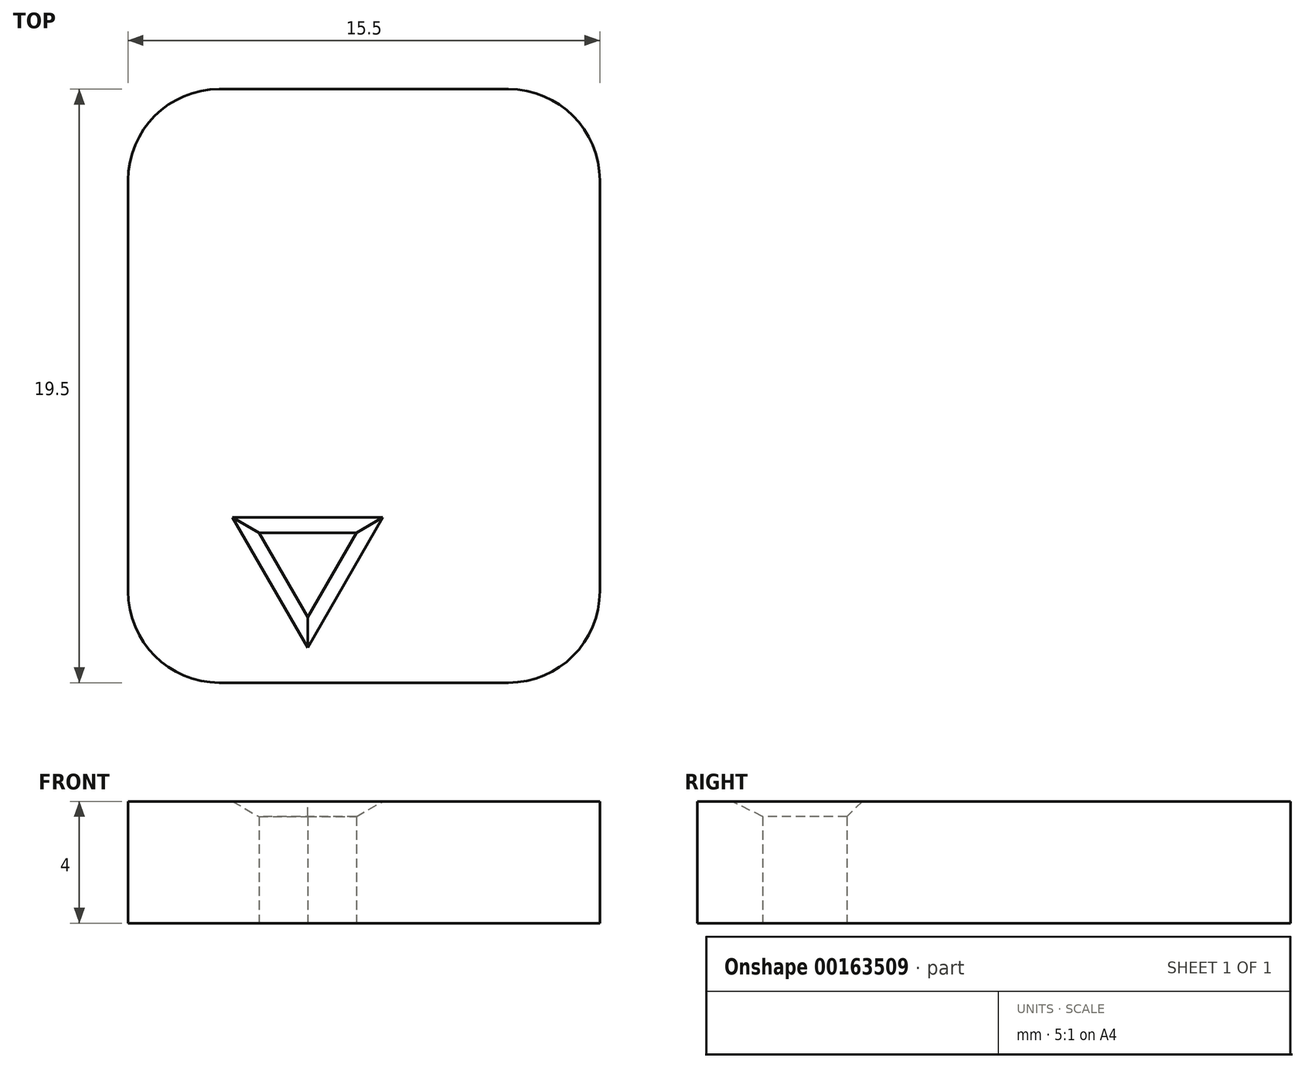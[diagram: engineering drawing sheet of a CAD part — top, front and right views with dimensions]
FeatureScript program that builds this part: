
annotation { "Feature Type Name" : "Feature", "Feature Type Description" : "" }
export const myFeature = defineFeature(function(context is Context, id is Id, definition is map)
    precondition{}
    {
        {
            var Q0;
            Q0=qCreatedBy(makeId("Top.planeOp"),FACE);
            var sketch = newSketch(context, id + "F0", { "sketchPlane" : qUnion([Q0])});
            skLineSegment(sketch, "E0.bottom", {"start": v(-15.5, 0) * mm, "end": v(0, 0) * mm});
            skLineSegment(sketch, "E0.top", {"start": v(-15.5, 19.5) * mm, "end": v(0, 19.5) * mm});
            skLineSegment(sketch, "E0.left", {"start": v(0, 0) * mm, "end": v(0, 19.5) * mm});
            skLineSegment(sketch, "E0.right", {"start": v(-15.5, 0) * mm, "end": v(-15.5, 19.5) * mm});
            skSolve(sketch);
        }
        {
            var Q0;
            Q0=qSketchRegion(id+"F0",true);
            extrude(context, id + "F1", {"entities" : qUnion([Q0]), "depth" : 4 * mm});
        }
        {
            var Q0;
            Q0=qCreatedBy(makeId("Top.planeOp"),FACE);
            var sketch = newSketch(context, id + "F2", { "sketchPlane" : qUnion([Q0])});
            skLineSegment(sketch, "E1.0", {"start": v(-15.5, 0) * mm, "end": v(-15.5, 19.5) * mm, "construction": true});
            skLineSegment(sketch, "E2", {"start": v(0, 4) * mm, "end": v(-15.5, 4) * mm, "construction": true});
            skLineSegment(sketch, "E3", {"start": v(-9.6, 0) * mm, "end": v(-9.6, 4) * mm, "construction": true});
            skCircle(sketch, "E4.cCircle", {"center": v(-9.6, 4) * mm, "radius": 1.85 * mm, "construction": true});
            skLineSegment(sketch, "E4.0", {"start": v(-9.6, 2.15) * mm, "end": v(-11.2, 4.93) * mm});
            skLineSegment(sketch, "E4.1", {"start": v(-11.2, 4.92) * mm, "end": v(-8, 4.92) * mm});
            skLineSegment(sketch, "E4.2", {"start": v(-8, 4.92) * mm, "end": v(-9.6, 2.15) * mm});
            skCircle(sketch, "E5", {"center": v(-9.6, 4) * mm, "radius": 1.5 * mm, "construction": true});
            skSolve(sketch);
        }
        {
            var Q0;
            Q0=qSketchRegion(id+"F2",true);
            extrude(context, id + "F3", {"entities" : qUnion([Q0]), "operationType" : NewBodyOperationType.REMOVE, "endBound" : BoundingType.THROUGH_ALL, "depth" : 25 * mm});
        }
        {
            var Q0;
            Q0=makeQuery(id+"F3.boolean.opBoolean","INTERSECT",EDGE,{"derivedFrom":[makeQuery(id+"F1.opExtrude","CAP_FACE",FACE,{"disambiguationData":[OSD([sQuery(id+"F0.wireOp",EDGE,"E0.bottom"),sQuery(id+"F0.wireOp",EDGE,"E0.top"),sQuery(id+"F0.wireOp",EDGE,"E0.left"),sQuery(id+"F0.wireOp",EDGE,"E0.right")])],"isStart":false}),makeQuery(id+"F3.opExtrude","SWEPT_FACE",FACE,{"disambiguationData":[OSD([sQuery(id+"F2.wireOp",EDGE,"E4.1")])]})]});
            var Q1;
            Q1=makeQuery(id+"F3.boolean.opBoolean","INTERSECT",EDGE,{"derivedFrom":[makeQuery(id+"F1.opExtrude","CAP_FACE",FACE,{"disambiguationData":[OSD([sQuery(id+"F0.wireOp",EDGE,"E0.bottom"),sQuery(id+"F0.wireOp",EDGE,"E0.top"),sQuery(id+"F0.wireOp",EDGE,"E0.left"),sQuery(id+"F0.wireOp",EDGE,"E0.right")])],"isStart":false}),makeQuery(id+"F3.opExtrude","SWEPT_FACE",FACE,{"disambiguationData":[OSD([sQuery(id+"F2.wireOp",EDGE,"E4.0")])]})]});
            var Q2;
            Q2=makeQuery(id+"F3.boolean.opBoolean","INTERSECT",EDGE,{"derivedFrom":[makeQuery(id+"F1.opExtrude","CAP_FACE",FACE,{"disambiguationData":[OSD([sQuery(id+"F0.wireOp",EDGE,"E0.bottom"),sQuery(id+"F0.wireOp",EDGE,"E0.top"),sQuery(id+"F0.wireOp",EDGE,"E0.left"),sQuery(id+"F0.wireOp",EDGE,"E0.right")])],"isStart":false}),makeQuery(id+"F3.opExtrude","SWEPT_FACE",FACE,{"disambiguationData":[OSD([sQuery(id+"F2.wireOp",EDGE,"E4.2")])]})]});
            chamfer(context, id + "F4", {"entities" : qUnion([Q0, Q1, Q2]), "width" : 0.5 * mm, "tangentPropagation" : true});
        }
        {
            var Q0;
            Q0=makeQuery(id+"F1.opExtrude","SWEPT_EDGE",EDGE,{"disambiguationData":[OSD([sQuery(id+"F0.wireOp",EDGE,"E0.bottom"),sQuery(id+"F0.wireOp",EDGE,"E0.right")])]});
            var Q1;
            Q1=makeQuery(id+"F1.opExtrude","SWEPT_EDGE",EDGE,{"disambiguationData":[OSD([sQuery(id+"F0.wireOp",EDGE,"E0.bottom"),sQuery(id+"F0.wireOp",EDGE,"E0.left")])]});
            var Q2;
            Q2=makeQuery(id+"F1.opExtrude","SWEPT_EDGE",EDGE,{"disambiguationData":[OSD([sQuery(id+"F0.wireOp",EDGE,"E0.top"),sQuery(id+"F0.wireOp",EDGE,"E0.left")])]});
            var Q3;
            Q3=makeQuery(id+"F1.opExtrude","SWEPT_EDGE",EDGE,{"disambiguationData":[OSD([sQuery(id+"F0.wireOp",EDGE,"E0.top"),sQuery(id+"F0.wireOp",EDGE,"E0.right")])]});
            fillet(context, id + "F5", {"entities" : qUnion([Q0, Q1, Q2, Q3]), "radius" : 3 * mm, "tangentPropagation" : true, "allowEdgeOverflow" : false});
        }
    });
